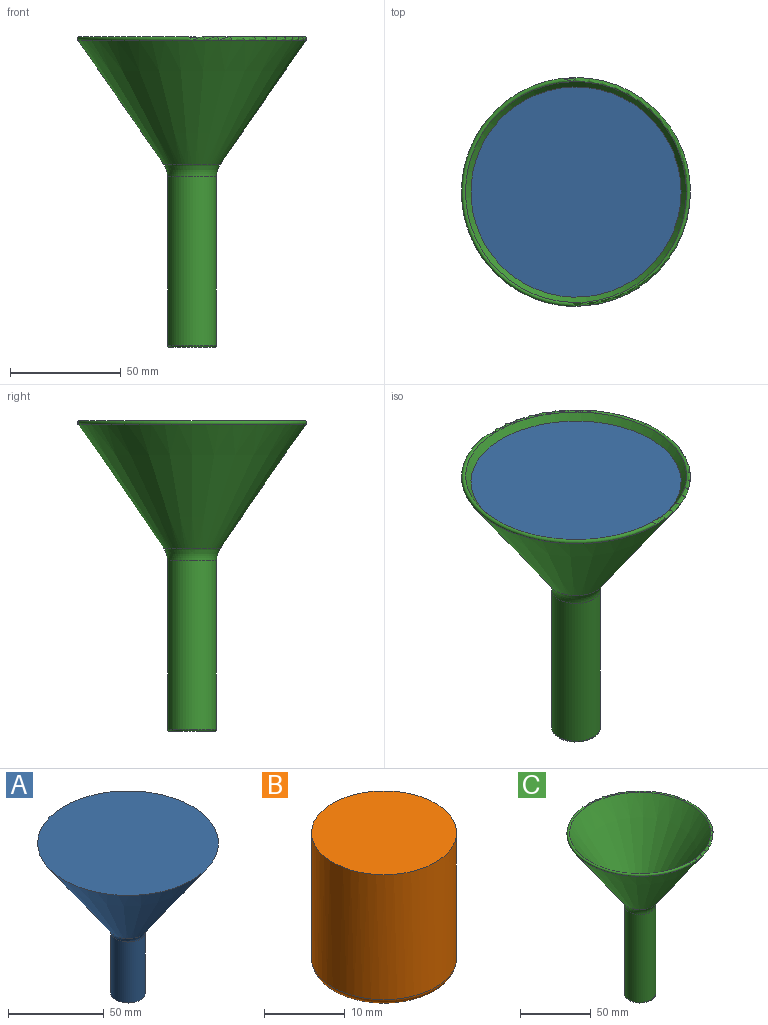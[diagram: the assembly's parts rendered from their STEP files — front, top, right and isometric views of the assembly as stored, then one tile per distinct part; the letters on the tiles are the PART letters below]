
ASSEMBLY  parts=3 mates=2
PART A: 5 faces, bbox 94.7x94.7x96.1 mm
  f0: plane 94.73x94.73mm, normal (0,0,1), area 7047.3mm2, adj f1
  f1: cone r=47.36mm half-angle=34.7deg, axis (0,0,1), area 11846.5mm2, adj f0,f2
  f2: torus R=14mm, axis (0,0,1), area 176.8mm2, adj f1,f3
  f3: cylinder r=9mm len=39.09mm, axis (0,0,1), area 2210.3mm2, adj f2,f4
  f4: plane 18x18mm, normal (0,0,-1), area 254.5mm2, adj f3
PART B: 6 faces, bbox 19.5x19.5x20 mm
  f0: plane 18x18mm, normal (0,0,1), area 254.5mm2, adj f1
  f1: cylinder r=9mm len=19mm, axis (0,0,1), area 1074.4mm2, adj f0,f5
  f2: cylinder r=7mm len=16.5mm, axis (0,0,1), area 725.7mm2, adj f4,f5
  f3: plane 13x13mm, normal (0,0,-1), area 132.7mm2, adj f4
  f4: torus R=6.5mm, axis (0,0,1), area 33.6mm2, adj f2,f3
  f5: torus R=8mm, axis (0,0,-1), area 157.9mm2, adj f1,f2
PART C: 8 faces, bbox 111.7x111.7x140 mm
  f0: cylinder r=9mm len=78.06mm, axis (0,0,-1), area 4414.4mm2, adj f4,f6
  f1: cone r=9mm half-angle=34.7deg, axis (0,0,1), area 13140mm2, adj f5,f6
  f2: cone r=11mm half-angle=34.7deg, axis (0,0,1), area 13697.7mm2, adj f5,f7
  f3: cylinder r=11mm len=75.88mm, axis (0,0,-1), area 5244.4mm2, adj f4,f7
  f4: torus R=10mm, axis (0,0,-1), area 197.4mm2, adj f0,f3
  f5: torus R=50.59mm, axis (0,0,1), area 1005.8mm2, adj f1,f2
  f6: torus R=14mm, axis (0,0,1), area 176.8mm2, adj f0,f1
  f7: torus R=21mm, axis (0,0,-1), area 441mm2, adj f2,f3
PLACE A t=(-33.18,23.14,-6.54)mm
PLACE B t=(-33.18,23.14,18.75)mm
PLACE C t=(-33.18,23.14,-6.77)mm
MATE slider B.f1 <-> C.f0  axis (0,0,1) through (-33.18,23.14,23.96)mm
MATE revolute A.f1 <-> B.f1  axis (0,0,-1) through (-33.18,23.14,33.46)mm
